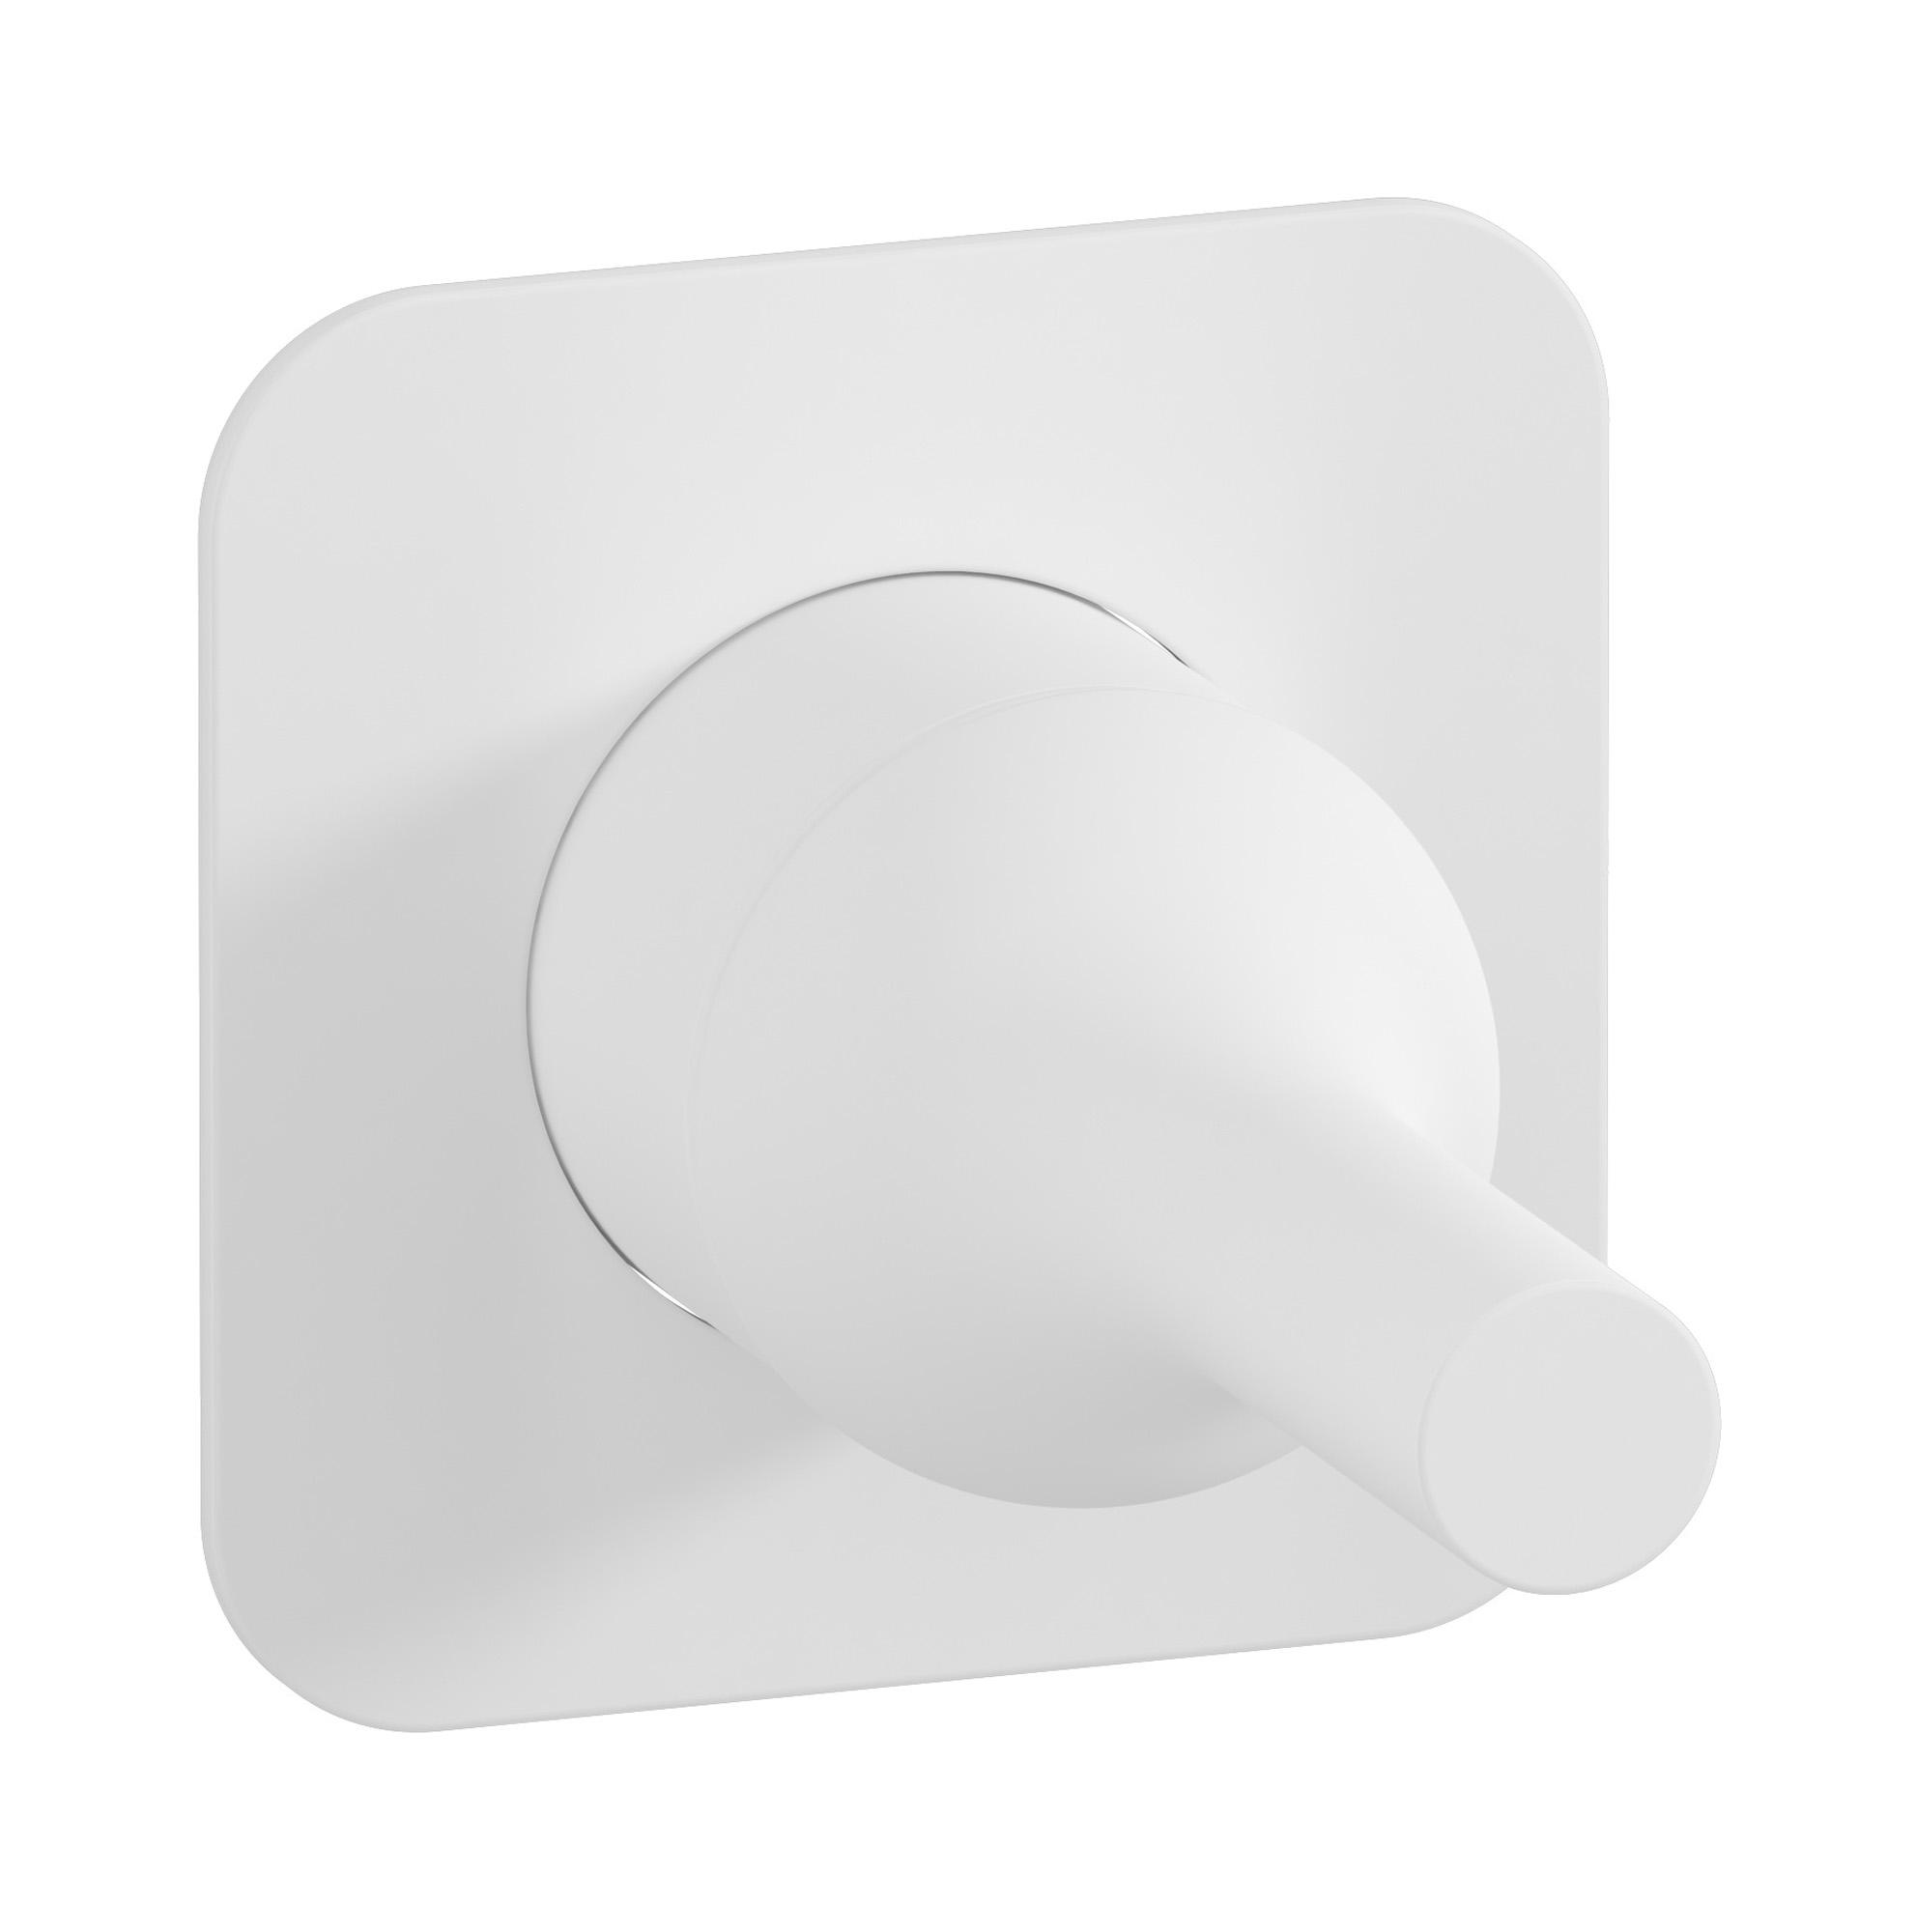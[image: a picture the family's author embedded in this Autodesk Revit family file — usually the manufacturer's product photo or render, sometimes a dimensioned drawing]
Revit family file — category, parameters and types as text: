
# Revit family: BI300
name_source: partatom
category: Apparecchi idraulici
units: mm (PartAtom-declared; Revit-internal decimal feet)

## family parameters
Basato su piano di lavoro = No
Condiviso = No
Mantieni orientamento annotazione = No
Numero OmniClass = 23.45.55.17
Punto di calcolo locali = No
Quota connettore circolare = Usa diametro
Sempre verticale = Sì
Taglio con vuoti quando caricato = No
Tipo di parte = Normale
Titolo OmniClass = Mixing Faucets

## types (4) — shared parameters
Cold water inlet = 10 mm  [stored 0.0328084 ft]
Commenti sul tipo = Wall mixer
Connessione CW = No
Connessione HW = No
Connessione di scarico = No
Connessione di ventilazione = No
Descrizione = Exposed parts for manual wall mixer
Hot water inlet = 10 mm  [stored 0.0328084 ft]
Produttore = IB Rubinetterie S.p.A.
URL = https://www.weareib.it
zero-valued in all types: Prospetto di default

## per-type parameters (varying)
| type | Finishes surface | Immagine tipo | Modello |
| Chrome | IB_Chrome | BI300CC.jpg | BI300CC |
| Brushed nickel | IB_Brushed nickel | BI300SS.jpg | BI300SS |
| Matt black | IB_matt black | BI300NP.jpg | BI300NP |
| Matt white | IB_matt white | BI300BO.jpg | BI300BO |

note: [stored X ft] marks values corroborated as IEEE doubles in the binary element streams (Revit-internal decimal feet)
